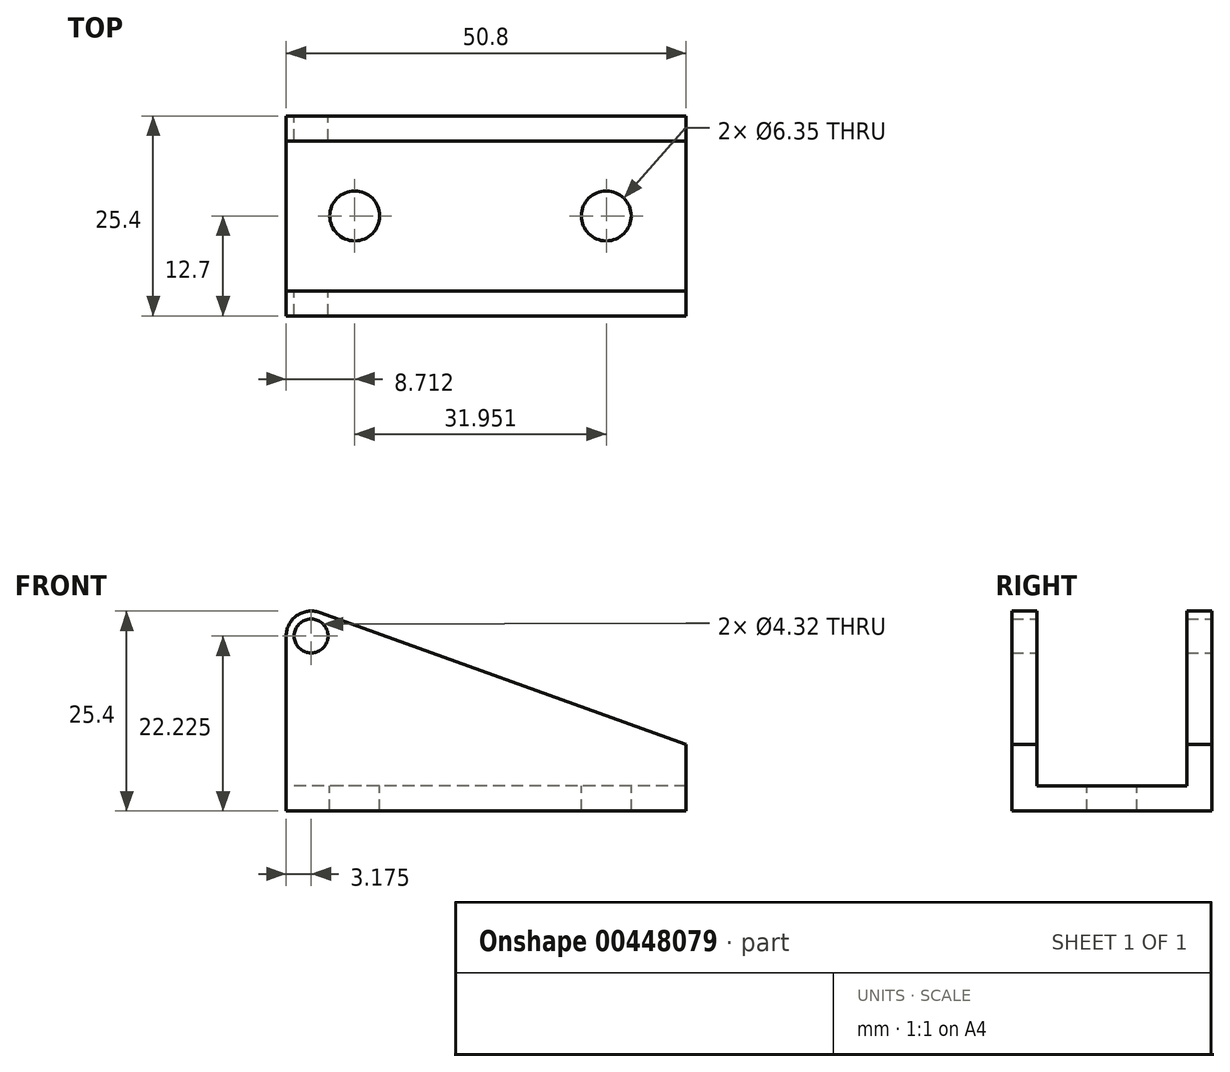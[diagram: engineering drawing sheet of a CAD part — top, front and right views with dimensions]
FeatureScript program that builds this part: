
annotation { "Feature Type Name" : "Feature", "Feature Type Description" : "" }
export const myFeature = defineFeature(function(context is Context, id is Id, definition is map)
    precondition{}
    {
        {
            var Q0;
            Q0=qCreatedBy(makeId("Front.planeOp"),FACE);
            var sketch = newSketch(context, id + "F0", { "sketchPlane" : qUnion([Q0])});
            skLineSegment(sketch, "E0.bottom", {"start": v(-25.4, 12.7) * mm, "end": v(25.4, 12.7) * mm});
            skLineSegment(sketch, "E0.top", {"start": v(-25.4, -12.7) * mm, "end": v(25.4, -12.7) * mm});
            skLineSegment(sketch, "E0.left", {"start": v(-25.4, 12.7) * mm, "end": v(-25.4, -12.7) * mm});
            skLineSegment(sketch, "E0.right", {"start": v(25.4, 12.7) * mm, "end": v(25.4, -12.7) * mm});
            skPoint(sketch, "E0.middle", {"position": v(0, 0) * mm});
            skCircle(sketch, "E1", {"center": v(-22.23, 9.53) * mm, "radius": 2.16 * mm});
            skArc(sketch, "E2", {"start": v(-25.4, 9.53) * mm, "mid": v(-24.05, 12.12) * mm, "end": v(-21.15, 12.51) * mm});
            skLineSegment(sketch, "E3", {"start": v(-21.15, 12.51) * mm, "end": v(25.4, -4.23) * mm});
            skSolve(sketch);
        }
        {
            var Q0;
            {var subQ1=sQuery(id+"F0.wireOp",EDGE,"E0.top");Q0=makeQuery(id+"F0.imprint","IMPRINT",FACE,{"disambiguationData":[TD([[makeQuery(id+"F0.imprint","IMPRINT",EDGE,{"derivedFrom":subQ1}),1.0]])]});}
            extrude(context, id + "F1", {"entities" : qUnion([Q0]), "depth" : 25.4 * mm});
        }
        {
            var Q0;
            Q0=makeQuery(id+"F1.opExtrude","SWEPT_FACE",FACE,{"disambiguationData":[OSD([sQuery(id+"F0.wireOp",EDGE,"E0.left")])]});
            var sketch = newSketch(context, id + "F2", { "sketchPlane" : qUnion([Q0])});
            skLineSegment(sketch, "E4", {"start": v(0, -9.53) * mm, "end": v(25.4, -9.53) * mm});
            skLineSegment(sketch, "E5", {"start": v(3.18, -12.7) * mm, "end": v(3.18, 15.97) * mm});
            skLineSegment(sketch, "E6", {"start": v(22.23, -12.7) * mm, "end": v(22.22, 16.48) * mm});
            skLineSegment(sketch, "E7", {"start": v(3.17, 15.97) * mm, "end": v(22.22, 16.48) * mm});
            skSolve(sketch);
        }
        {
            var Q0;
            Q0 = qSketchRegion(id + "F2", true);
            extrude(context, id + "F3", {"entities" : qUnion([Q0]), "operationType" : NewBodyOperationType.REMOVE, "endBound" : BoundingType.THROUGH_ALL, "oppositeDirection" : true, "depth" : 25.4 * mm});
        }
        {
            var Q0;
            Q0=makeQuery(id+"F3.boolean.opBoolean","COPY",FACE,{"derivedFrom":makeQuery(id+"F3.opExtrude","SWEPT_FACE",FACE,{"disambiguationData":[OSD([sQuery(id+"F2.wireOp",EDGE,"E4")])]})});
            var sketch = newSketch(context, id + "F4", { "sketchPlane" : qUnion([Q0])});
            skCircle(sketch, "E8", {"center": v(-16.69, -12.7) * mm, "radius": 3.18 * mm});
            skPoint(sketch, "E8.centerSnap0", {"position": v(-25.4, -12.7) * mm});
            skCircle(sketch, "E9", {"center": v(15.26, -12.7) * mm, "radius": 3.18 * mm});
            skSolve(sketch);
        }
        {
            var Q0;
            Q0 = qSketchRegion(id + "F4", true);
            extrude(context, id + "F5", {"entities" : qUnion([Q0]), "operationType" : NewBodyOperationType.REMOVE, "oppositeDirection" : true, "depth" : 25.4 * mm});
        }
    });
